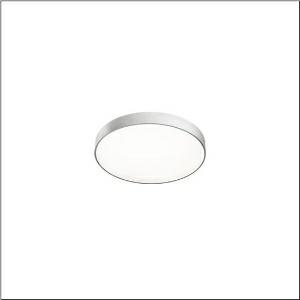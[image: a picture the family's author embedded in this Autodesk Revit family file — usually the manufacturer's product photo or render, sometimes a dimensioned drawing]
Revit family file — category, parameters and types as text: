
# Revit family: round_21_s_51mr34fd0421s
name_source: partatom
category: Lighting Fixtures
units: mm (PartAtom-declared; Revit-internal decimal feet)

## family parameters
Cut with Voids When Loaded = No
Host = Face
Light Source = No
Part Type = Normal
Room Calculation Point = No
Round Connector Dimension = Use Diameter
Shared = No

## types (1)
- Round 21 S (1 x LED, 3910 lm, 30.3 W, 4000K)
    Apparent Load = 30 VA
    CIE Flux Codes = 49 80 96 100 100
    Color Rendering = 80
    Color Temperature = 4000K
    Default Elevation = 1800 mm
    Description = Round 21 S, wall and ceiling luminaire, primary optical cover: cover, of PMMA, opal, light emission: direct distribution, primary light characteristic: symmetric, installation type: suspended mounting, surface-mounted, LED, rated luminous flux: 3.900lm, luminous efficacy: 129lm/W, light colour: 840, colour temperature: 4000K, control gear: DALI 2, with terminal, 5-pole, mains connection: 230V, AC, 50/60Hz, rated input power: 30.3W, housing, of aluminium, coated, silver, diameter: 400mm, height: 62mm, protection rating (complete): IP40, insulation class (complete): insulation class I (protective earthing), certification: CE, impact resistance: IK04, permissible operating ambient temperature: -10..+35°C, packaging unit: 1 piece
    Height = 87 mm
    Lamp = 1 x LED
    Lamp Light Flux = 3910 lm
    Lamp Power = 30.3 W
    Lamp count = 1
    Length = 400 mm
    Luminous efficacy = 129 lm/W
    Manufacturer = Siteco
    ModVariant = No
    Model = 51MR34FD0421S
    Mounting Place = Ceiling
    Mounting Type = Surface mounted
    Number of Poles = 1
    OnlyDefault = Yes
    Power Factor = 1
    Product Name = Round 21 S
    Product group = wall and ceiling luminaire | ceiling mounted
    ProductGroupID = 304
    Protection Class = Protection class I
    Protection Degree = IP 40
    RLX_Detail_Level = 1
    RLX_Emergency_Light_Flux = 0 lm
    RLX_Emergency_Type = 0
    RLX_Emergency_Type_DB = No
    RlxData = <blob elided: 11149 chars, md5=5eb6bb9c>
    Socket = socket
    Standby Power = 0 W
    System Light Flux = 3910 lm
    System Power = 30 W
    Type Comments = Product without accessories
    Type Image = l_1258309.jpg
    URL = http://relux.com
    VarID = ---
    Voltage = 0 V
    Weight = 0.00 kg
    Width = 0 mm  [stored 0 ft]

note: [stored X ft] marks values corroborated as IEEE doubles in the binary element streams (Revit-internal decimal feet)

## geometry (parser evidence)
native form markers: Sweep x10
no freeform markers — native parametric forms only
